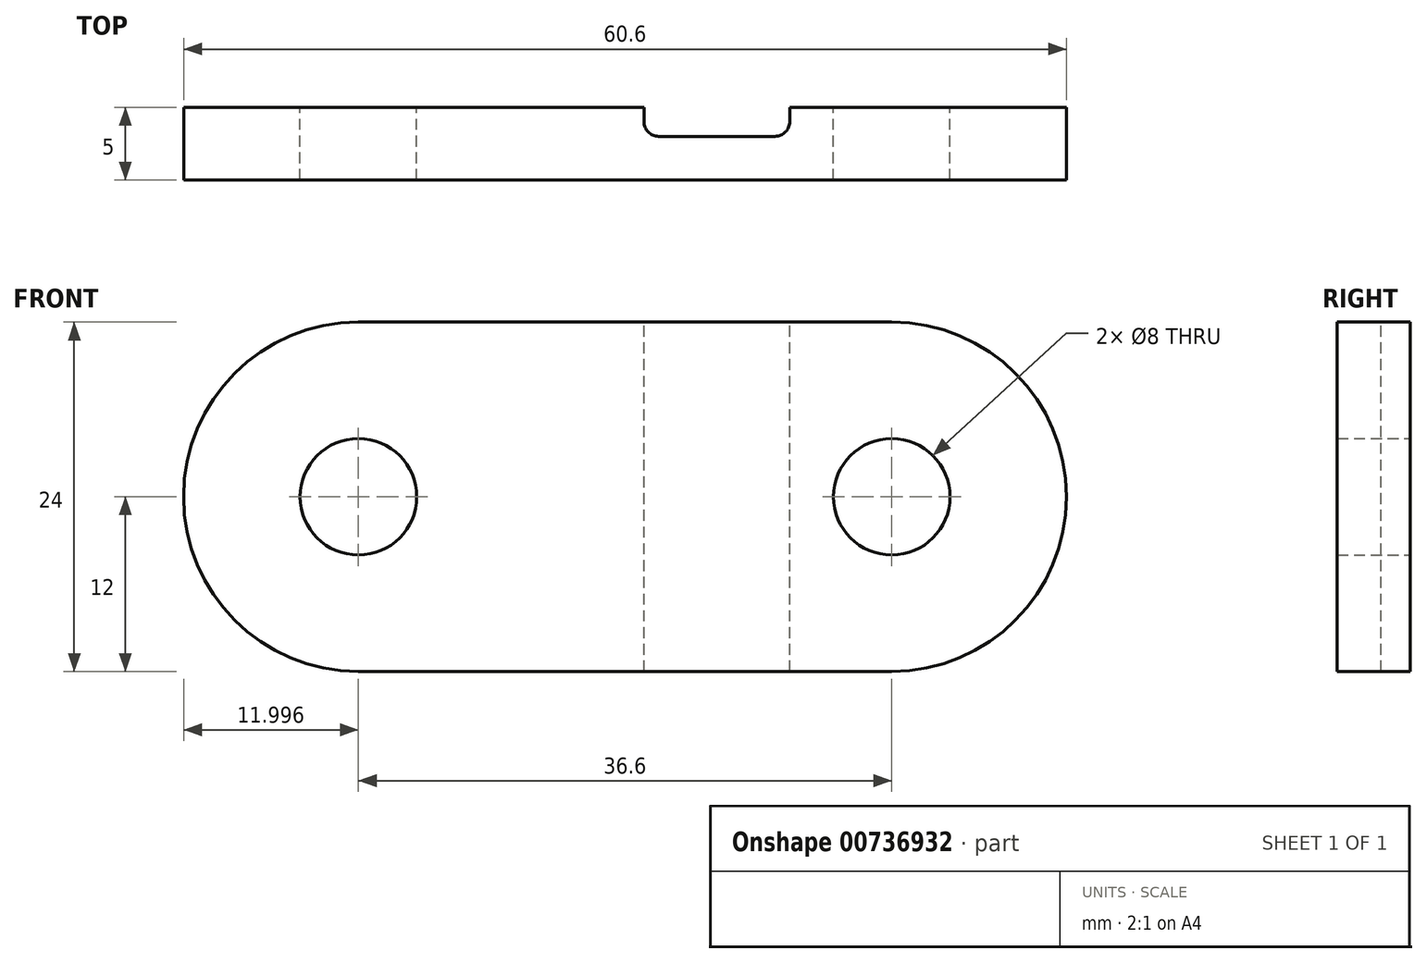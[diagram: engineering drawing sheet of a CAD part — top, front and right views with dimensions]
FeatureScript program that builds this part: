
annotation { "Feature Type Name" : "Feature", "Feature Type Description" : "" }
export const myFeature = defineFeature(function(context is Context, id is Id, definition is map)
    precondition{}
    {
        {
            var Q0;
            Q0=qCreatedBy(makeId("Front.planeOp"),FACE);
            var sketch = newSketch(context, id + "F0", { "sketchPlane" : qUnion([Q0])});
            skCircle(sketch, "E0", {"center": v(-21.76, 0) * mm, "radius": 4 * mm});
            skCircle(sketch, "E1", {"center": v(14.84, 0) * mm, "radius": 4 * mm});
            skArc(sketch, "E2", {"start": v(-21.76, 12) * mm, "mid": v(-33.76, 0) * mm, "end": v(-21.76, -12) * mm});
            skArc(sketch, "E3", {"start": v(14.84, -12) * mm, "mid": v(26.84, 0) * mm, "end": v(14.84, 12) * mm});
            skLineSegment(sketch, "E4", {"start": v(14.84, 25.74) * mm, "end": v(14.84, -32.09) * mm, "construction": true});
            skLineSegment(sketch, "E5", {"start": v(-21.76, 25.15) * mm, "end": v(-21.76, -27.9) * mm, "construction": true});
            skLineSegment(sketch, "E6", {"start": v(-21.76, 12) * mm, "end": v(14.84, 12) * mm});
            skLineSegment(sketch, "E7", {"start": v(-21.76, -12) * mm, "end": v(14.84, -12) * mm});
            skSolve(sketch);
        }
        {
            var Q0;
            Q0 = qSketchRegion(id + "F0", true);
            extrude(context, id + "F1", {"entities" : qUnion([Q0]), "depth" : 5 * mm, "offsetDistance" : 25 * mm});
        }
        {
            var Q0;
            Q0=makeQuery(id+"F1.opExtrude","SWEPT_FACE",FACE,{"disambiguationData":[OSD([sQuery(id+"F0.wireOp",EDGE,"E6")])]});
            var sketch = newSketch(context, id + "F2", { "sketchPlane" : qUnion([Q0])});
            skLineSegment(sketch, "E8", {"start": v(-10.04, -2) * mm, "end": v(36.07, -2) * mm, "construction": true});
            skLineSegment(sketch, "E9", {"start": v(2.84, 6.98) * mm, "end": v(2.84, -13.1) * mm, "construction": true});
            skLineSegment(sketch, "E10.bottom", {"start": v(-2.16, 0) * mm, "end": v(7.84, 0) * mm});
            skLineSegment(sketch, "E10.top", {"start": v(-2.16, -2) * mm, "end": v(7.84, -2) * mm});
            skLineSegment(sketch, "E10.left", {"start": v(-2.16, 0) * mm, "end": v(-2.16, -2) * mm});
            skLineSegment(sketch, "E10.right", {"start": v(7.84, 0) * mm, "end": v(7.84, -2) * mm});
            skSolve(sketch);
        }
        {
            var Q0;
            Q0 = qSketchRegion(id + "F2", true);
            extrude(context, id + "F3", {"entities" : qUnion([Q0]), "operationType" : NewBodyOperationType.REMOVE, "endBound" : BoundingType.THROUGH_ALL, "oppositeDirection" : true, "depth" : 25 * mm, "offsetDistance" : 25 * mm});
        }
        {
            var Q0;
            Q0=makeQuery(id+"F3.boolean.opBoolean","COPY",EDGE,{"derivedFrom":makeQuery(id+"F3.opExtrude","SWEPT_EDGE",EDGE,{"disambiguationData":[OSD([sQuery(id+"F2.wireOp",EDGE,"E10.top"),sQuery(id+"F2.wireOp",EDGE,"E10.right")])]})});
            var Q1;
            Q1=makeQuery(id+"F3.boolean.opBoolean","COPY",EDGE,{"derivedFrom":makeQuery(id+"F3.opExtrude","SWEPT_EDGE",EDGE,{"disambiguationData":[OSD([sQuery(id+"F2.wireOp",EDGE,"E10.top"),sQuery(id+"F2.wireOp",EDGE,"E10.left")])]})});
            fillet(context, id + "F4", {"entities" : qUnion([Q0, Q1]), "radius" : 1 * mm, "tangentPropagation" : true, "allowEdgeOverflow" : false});
        }
    });
